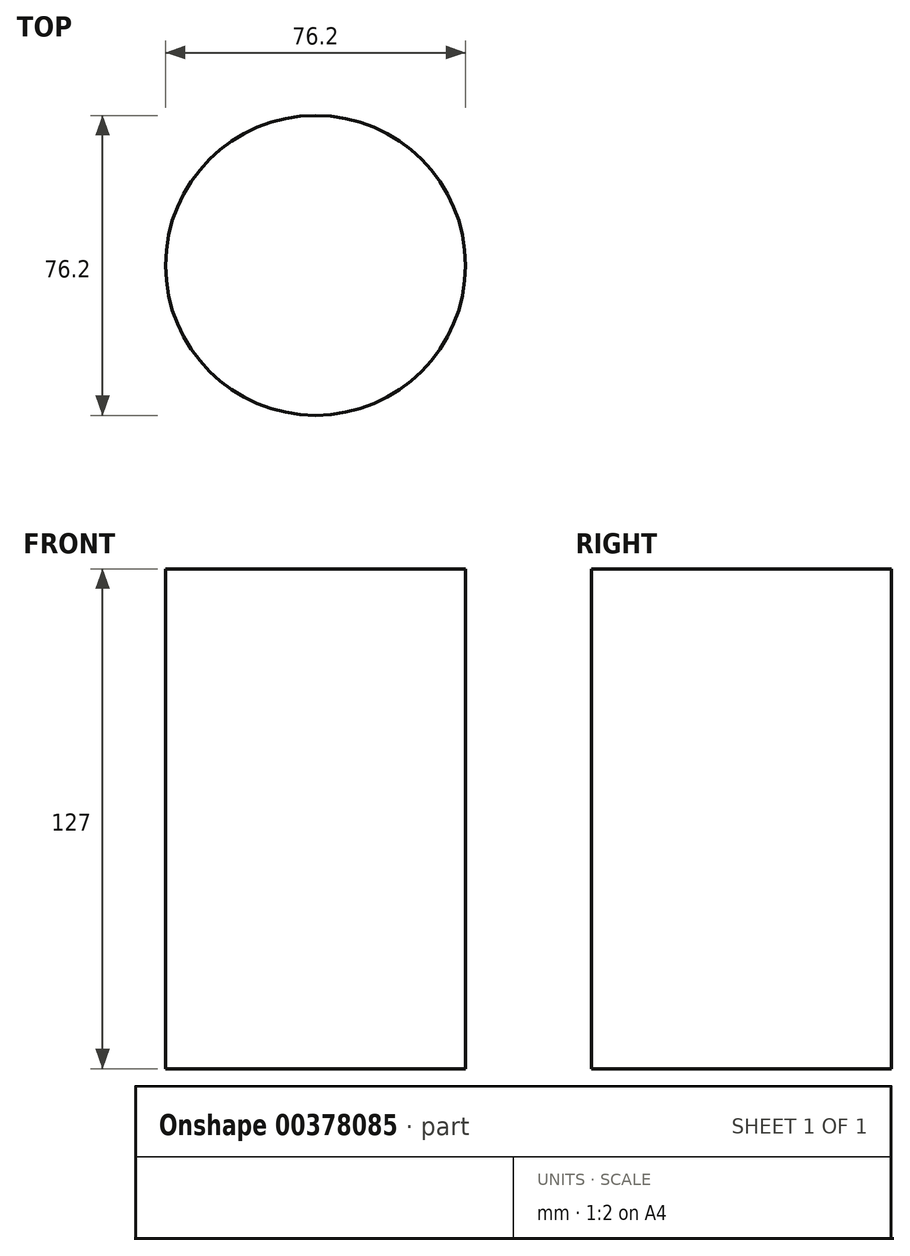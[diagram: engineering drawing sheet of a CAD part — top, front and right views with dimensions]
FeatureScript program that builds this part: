
annotation { "Feature Type Name" : "Feature", "Feature Type Description" : "" }
export const myFeature = defineFeature(function(context is Context, id is Id, definition is map)
    precondition{}
    {
        {
            var Q0;
            Q0=qCreatedBy(makeId("Top.planeOp"),FACE);
            var sketch = newSketch(context, id + "F0", { "sketchPlane" : qUnion([Q0])});
            skCircle(sketch, "E0", {"center": v(0, 0) * mm, "radius": 38.1 * mm});
            skSolve(sketch);
        }
        {
            var Q0;
            Q0=makeQuery(id+"F0.imprint","IMPRINT",FACE,{"disambiguationData":[TD([[makeQuery(id+"F0.imprint","IMPRINT",EDGE,{"derivedFrom":sQuery(id+"F0.wireOp",EDGE,"E0")}),1.0]])]});
            extrude(context, id + "F1", {"entities" : qUnion([Q0]), "depth" : 127 * mm});
        }
    });
